# Revit family: FAM1_63_UN_Spot_ETK
name_source: partatom
category: Lighting Fixtures
revit_build: Autodesk Revit 2017 (Build: 20190508_0315(x64)
units: mm (PartAtom-declared; Revit-internal decimal feet)

## family parameters
Always vertical = Yes
Cut with Voids When Loaded = Yes
Light Source = No
OmniClass Number = 23.80.70.11.14.11
OmniClass Title = Downlights
Part Type = Normal
Room Calculation Point = Yes
Round Connector Dimension = Use Diameter
Shared = No
Work Plane-Based = No

## types (9) — shared parameters
Apparent Load = 9 VA
Assembly Code = 63.0
Bundle = 42°
IfcExportAs = IfcLightFixtureType
IfcExportType = USERDEFINED
Lamp = LED
Manufacturer = ETK licht B.V.
Material = RAL 9003
Model = FAM.1
URL = https://www.etk.nl
Voltage = 230 V
Wattage Comments = 9W

## per-type parameters (varying)
| type | Light Source |
| FAM.1101.xx - 9W / 770lm / 2700K | FAM.1 - Lightsource : FAM.1101.xx - 9W / 770lm / 2700K |
| FAM.1201.xx - 9W / 830lm / 3000K | FAM.1 - Lightsource : FAM.1201.xx - 9W / 830lm / 3000K |
| FAM.1301.xx - 9W / 850lm / 4000K | FAM.1 - Lightsource : FAM.1301.xx - 9W / 850lm / 4000K |
| FAM.1102.xx - 9W / 770lm / 2700K | FAM.1 - Lightsource : FAM.1102.xx - 9W / 770lm / 2700K |
| FAM.1202.xx - 9W / 830lm / 3000K | FAM.1 - Lightsource : FAM.1202.xx - 9W / 830lm / 3000K |
| FAM.1302.xx - 9W / 850lm / 4000K | FAM.1 - Lightsource : FAM.1302.xx - 9W / 850lm / 4000K |
| FAM.1103.xx - 9W / 770lm / 2700K | FAM.1 - Lightsource : FAM.1103.xx - 9W / 770lm / 2700K |
| FAM.1203.xx - 9W / 830lm / 3000K | FAM.1 - Lightsource : FAM.1203.xx - 9W / 830lm / 3000K |
| FAM.1303.xx - 9W / 850lm / 4000K | FAM.1 - Lightsource : FAM.1303.xx - 9W / 850lm / 4000K |

## geometry (parser evidence)
native form markers: Sweep x5
no freeform markers — native parametric forms only
